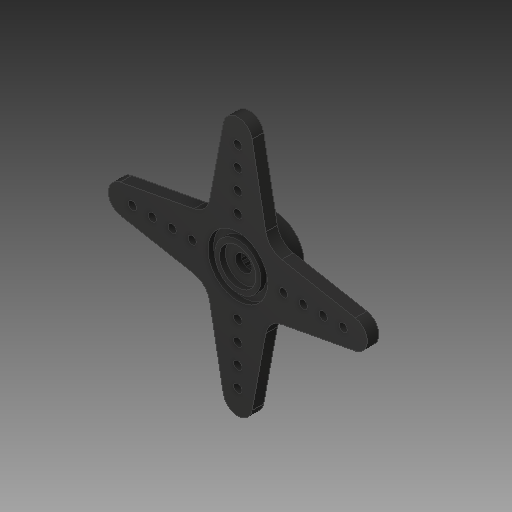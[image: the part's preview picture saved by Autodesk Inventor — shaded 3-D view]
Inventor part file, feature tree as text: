
AUTODESK INVENTOR PART (.ipt)
format: ipt  version: 2018.3 (Build 223284000, 284)  size: 193,536 bytes
history: native  units: mm
features: chamfer x1
ambient origin geometry x8: Origin, YZ Plane, XZ Plane, XY Plane, X Axis, Y Axis, Z Axis, Center Point
bodies: Solid1 (feature_tree)
feature tree (1):
  chamfer  "Chamfer2"  [1 undecoded]
note: 1 required parameter value undecoded (feature->parameter linkage not recoverable at this tier; creation-order binding heuristic only, values carry confidence <= 0.55)
